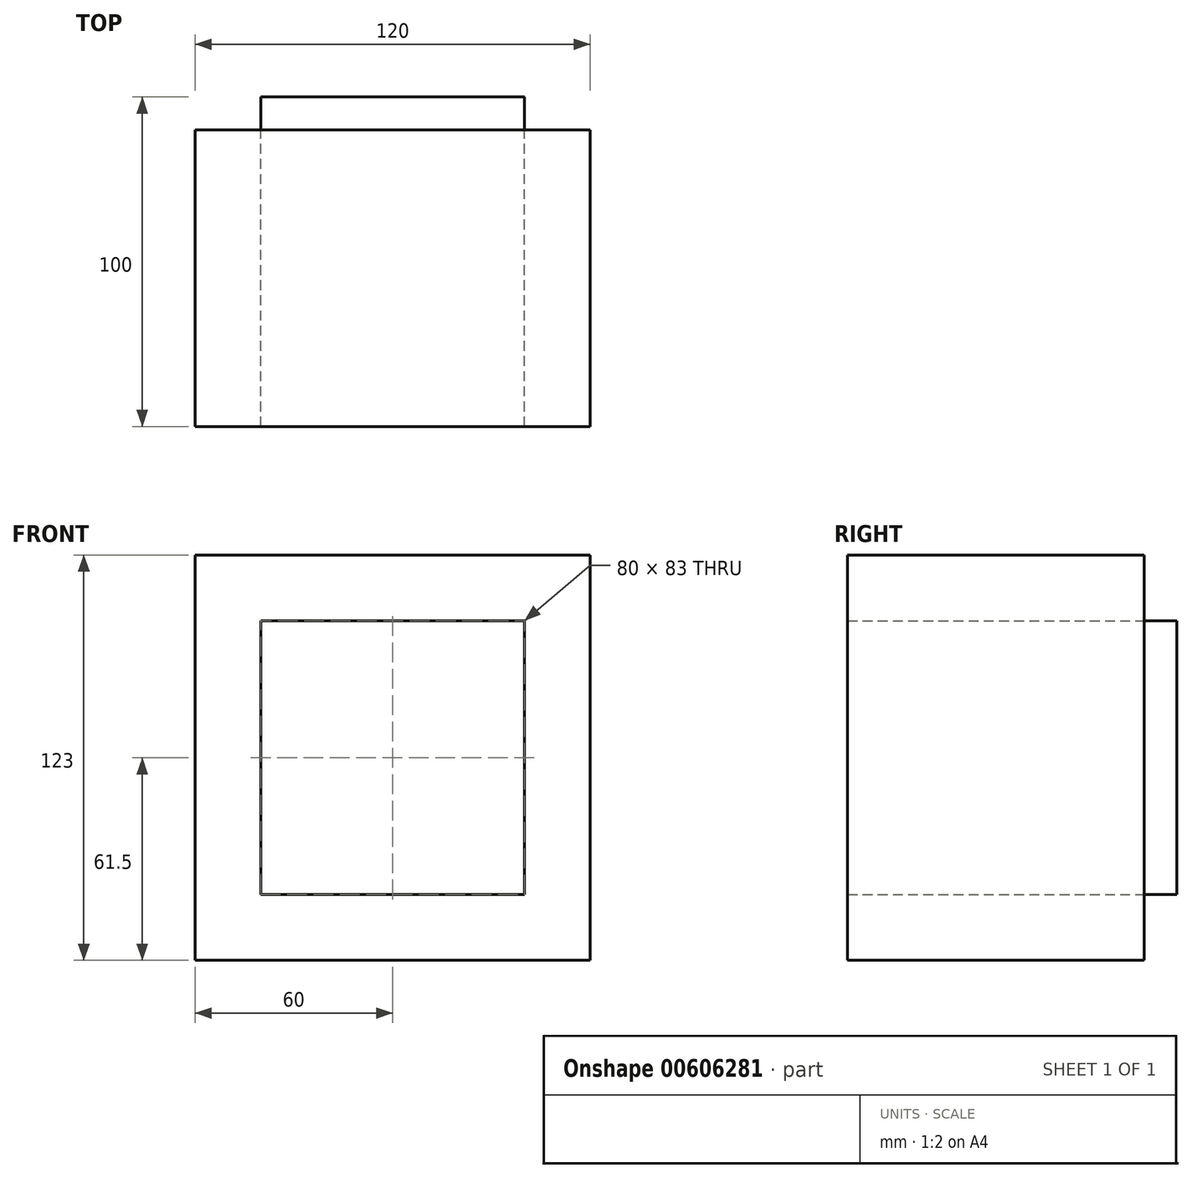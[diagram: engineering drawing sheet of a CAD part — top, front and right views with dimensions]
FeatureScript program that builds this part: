
annotation { "Feature Type Name" : "Feature", "Feature Type Description" : "" }
export const myFeature = defineFeature(function(context is Context, id is Id, definition is map)
    precondition{}
    {
        {
            var Q0;
            Q0=qCreatedBy(makeId("Front.planeOp"),FACE);
            cPlane(context, id + "F0", {"entities" : qUnion([Q0]), "cplaneType" : CPlaneType.OFFSET, "offset" : 21 * mm, "width" : 150 * mm, "height" : 150 * mm});
        }
        {
            var Q0;
            Q0=qCreatedBy(id+"F0.planeOp",FACE);
            var sketch = newSketch(context, id + "F1", { "sketchPlane" : qUnion([Q0])});
            skLineSegment(sketch, "E0.bottom", {"start": v(-40, -41.5) * mm, "end": v(40, -41.5) * mm});
            skLineSegment(sketch, "E0.top", {"start": v(-40, 41.5) * mm, "end": v(40, 41.5) * mm});
            skLineSegment(sketch, "E0.left", {"start": v(-40, -41.5) * mm, "end": v(-40, 41.5) * mm});
            skLineSegment(sketch, "E0.right", {"start": v(40, -41.5) * mm, "end": v(40, 41.5) * mm});
            skPoint(sketch, "E0.middle", {"position": v(0, 0) * mm});
            skLineSegment(sketch, "E1.bottom", {"start": v(-40, -1.5) * mm, "end": v(40, -1.5) * mm});
            skLineSegment(sketch, "E1.top", {"start": v(-40, 1.5) * mm, "end": v(40, 1.5) * mm});
            skLineSegment(sketch, "E1.left", {"start": v(-40, -1.5) * mm, "end": v(-40, 1.5) * mm});
            skLineSegment(sketch, "E1.right", {"start": v(40, -1.5) * mm, "end": v(40, 1.5) * mm});
            skSolve(sketch);
        }
        {
            var Q0;
            Q0 = qSketchRegion(id + "F1", true);
            extrude(context, id + "F2", {"entities" : qUnion([Q0]), "depth" : 100 * mm, "offsetDistance" : 25 * mm});
        }
        {
            var Q0;
            Q0=qCreatedBy(makeId("Front.planeOp"),FACE);
            cPlane(context, id + "F3", {"entities" : qUnion([Q0]), "cplaneType" : CPlaneType.OFFSET, "offset" : 31 * mm, "width" : 150 * mm, "height" : 150 * mm});
        }
        {
            var Q0;
            Q0=qCreatedBy(id+"F3.planeOp",FACE);
            var sketch = newSketch(context, id + "F4", { "sketchPlane" : qUnion([Q0])});
            skLineSegment(sketch, "E2.bottom", {"start": v(-60, -61.5) * mm, "end": v(60, -61.5) * mm});
            skLineSegment(sketch, "E2.top", {"start": v(-60, 61.5) * mm, "end": v(60, 61.5) * mm});
            skLineSegment(sketch, "E2.left", {"start": v(-60, -61.5) * mm, "end": v(-60, 61.5) * mm});
            skLineSegment(sketch, "E2.right", {"start": v(60, -61.5) * mm, "end": v(60, 61.5) * mm});
            skPoint(sketch, "E2.middle", {"position": v(0, 0) * mm});
            skLineSegment(sketch, "E3.bottom", {"start": v(-40, -41.5) * mm, "end": v(40, -41.5) * mm});
            skLineSegment(sketch, "E3.top", {"start": v(-40, 41.5) * mm, "end": v(40, 41.5) * mm});
            skLineSegment(sketch, "E3.left", {"start": v(-40, -41.5) * mm, "end": v(-40, 41.5) * mm});
            skLineSegment(sketch, "E3.right", {"start": v(40, -41.5) * mm, "end": v(40, 41.5) * mm});
            skSolve(sketch);
        }
        {
            var Q0;
            Q0 = qSketchRegion(id + "F4", true);
            extrude(context, id + "F5", {"entities" : qUnion([Q0]), "depth" : 90 * mm, "offsetDistance" : 25 * mm});
        }
    });
